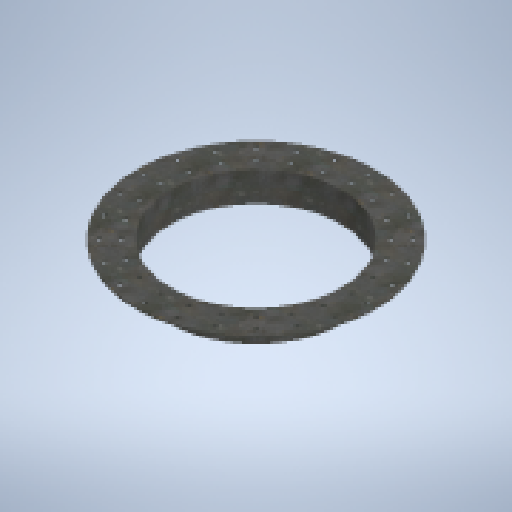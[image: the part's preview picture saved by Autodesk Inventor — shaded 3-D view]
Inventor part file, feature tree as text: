
AUTODESK INVENTOR PART (.ipt)
format: ipt  version: 2023 (Build 270158000, 158)  size: 246,272 bytes
history: native  units: in
note: dims shown in document units (in); Inventor stores cm internally (conversion verified against a paired STEP export)
features: sketch x2, revolve x1, extrude x1, pattern_circular x1
ambient origin geometry x8: Origin, YZ Plane, XZ Plane, XY Plane, X Axis, Y Axis, Z Axis, Center Point
bodies: Solid1 (feature_tree)
feature tree (5):
  revolve  "Revolution1"  [1 undecoded]
  extrude  "Extrusion1"  Depth=3.937in
  pattern_circular  "Circular Pattern1"  Count=10  [1 undecoded]
  sketch  "Sketch1"  dims[d0=0.2362in d1=0.2362in]
  sketch  "Sketch2"  dims[d2=24.0157in d3=33.0709in d4=3.937in d5=90.0deg d6=0.5625in d7=0.5625in d9=26.378in d10=30.7087in d11=0.0in d12=0.0in d13=9.4488in d14=360.0deg]
note: 2 required parameter values undecoded (feature->parameter linkage not recoverable at this tier; creation-order binding heuristic only, values carry confidence <= 0.55)